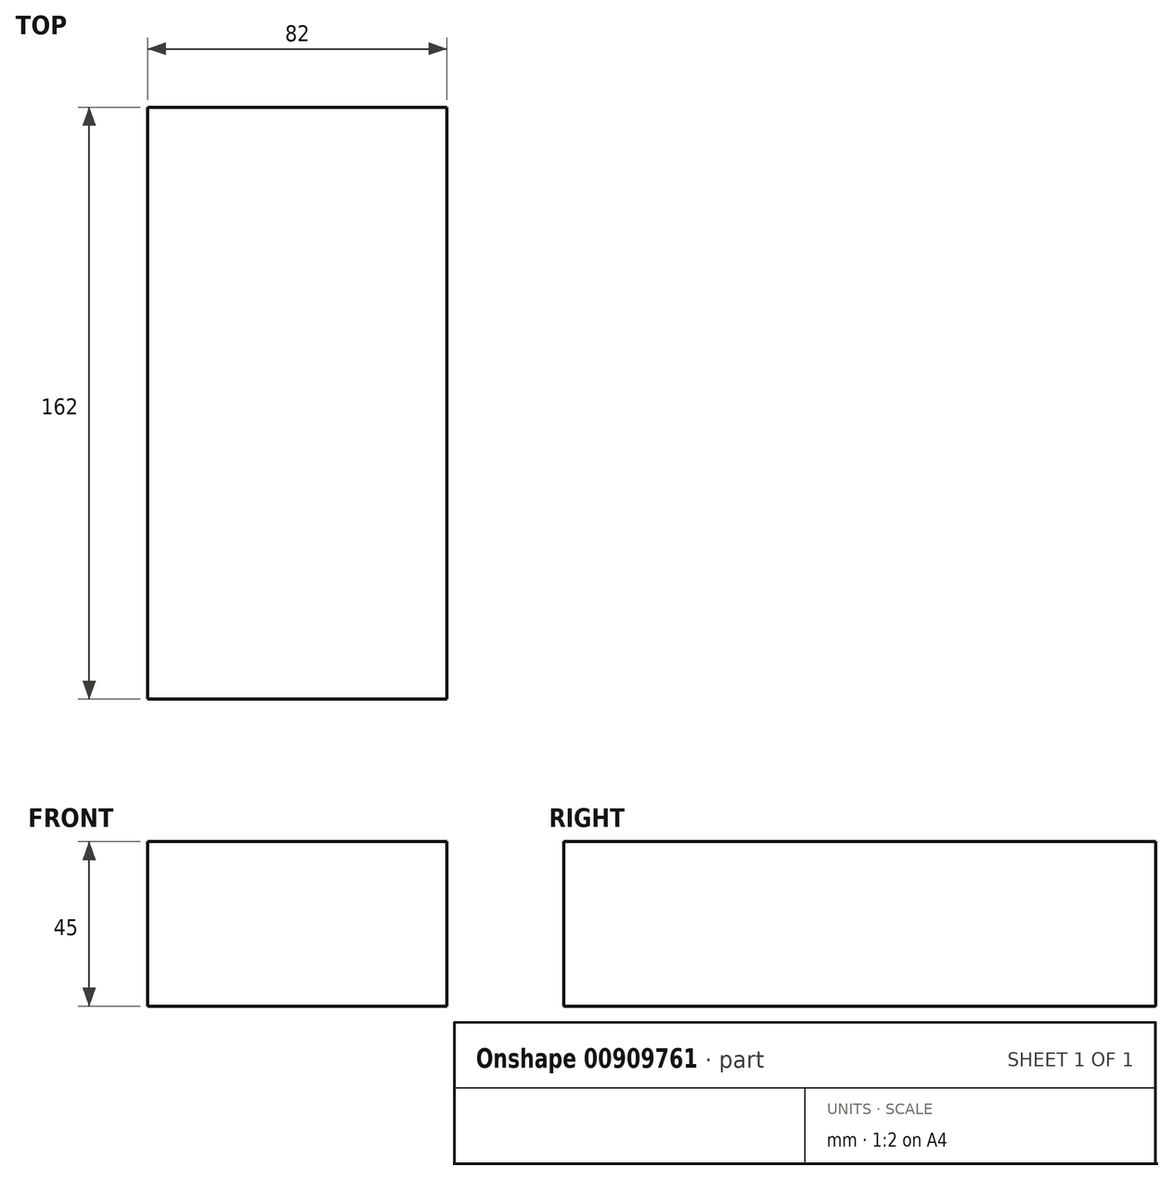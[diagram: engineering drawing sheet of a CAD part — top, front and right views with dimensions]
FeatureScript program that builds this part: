
annotation { "Feature Type Name" : "Feature", "Feature Type Description" : "" }
export const myFeature = defineFeature(function(context is Context, id is Id, definition is map)
    precondition{}
    {
        {
            var Q0;
            Q0=qCreatedBy(makeId("Top.planeOp"),FACE);
            var sketch = newSketch(context, id + "F0", { "sketchPlane" : qUnion([Q0])});
            skLineSegment(sketch, "E0.bottom", {"start": v(41, 81) * mm, "end": v(-41, 81) * mm});
            skLineSegment(sketch, "E0.top", {"start": v(41, -81) * mm, "end": v(-41, -81) * mm});
            skLineSegment(sketch, "E0.left", {"start": v(41, 81) * mm, "end": v(41, -81) * mm});
            skLineSegment(sketch, "E0.right", {"start": v(-41, 81) * mm, "end": v(-41, -81) * mm});
            skPoint(sketch, "E0.middle", {"position": v(0, 0) * mm});
            skSolve(sketch);
        }
        {
            var Q0;
            Q0 = qSketchRegion(id + "F0", true);
            extrude(context, id + "F1", {"entities" : qUnion([Q0]), "depth" : 45 * mm, "offsetDistance" : 25 * mm});
        }
    });
